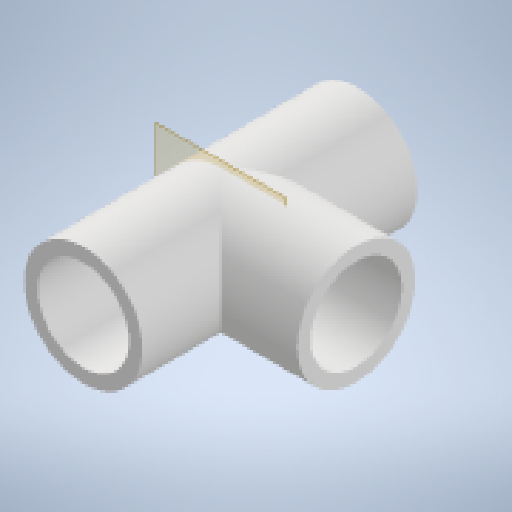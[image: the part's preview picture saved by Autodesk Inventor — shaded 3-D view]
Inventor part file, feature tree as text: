
AUTODESK INVENTOR PART (.ipt)
format: ipt  version: 2023.1 (Build 271208000, 208)  size: 265,728 bytes
history: native  units: mm
features: sketch x4, revolve x2, extrude x2, plane x1
ambient origin geometry x8: Origin, YZ Plane, XZ Plane, XY Plane, X Axis, Y Axis, Z Axis, Center Point
bodies: Solid1 (feature_tree)
feature tree (9):
  revolve  "Revolution1"  [1 undecoded]
  plane  "Work Plane1"
  revolve  "Revolution2"  [1 undecoded]
  extrude  "Extrusion1"  Depth=20.0mm
  extrude  "Extrusion2"  Depth=10.0mm
  sketch  "Sketch1"  dims[d0=65.0mm d1=3.2mm]
  sketch  "Sketch2"  dims[d2=0.4mm d3=20.0mm]
  sketch  "Sketch4"  dims[d4=0.4mm d6=20.0mm]
  sketch  "Sketch5"  dims[d7=28.0mm d8=0.5mm d9=0.4mm d10=90.0deg d11=28.0mm d12=3.2mm d13=0.5mm d14=0.4mm d15=20.0mm d16=46.0mm d17=90.0deg d18=10.0mm d19=0.0mm d20=10.0mm d21=0.0mm]
note: 2 required parameter values undecoded (feature->parameter linkage not recoverable at this tier; creation-order binding heuristic only, values carry confidence <= 0.55)
